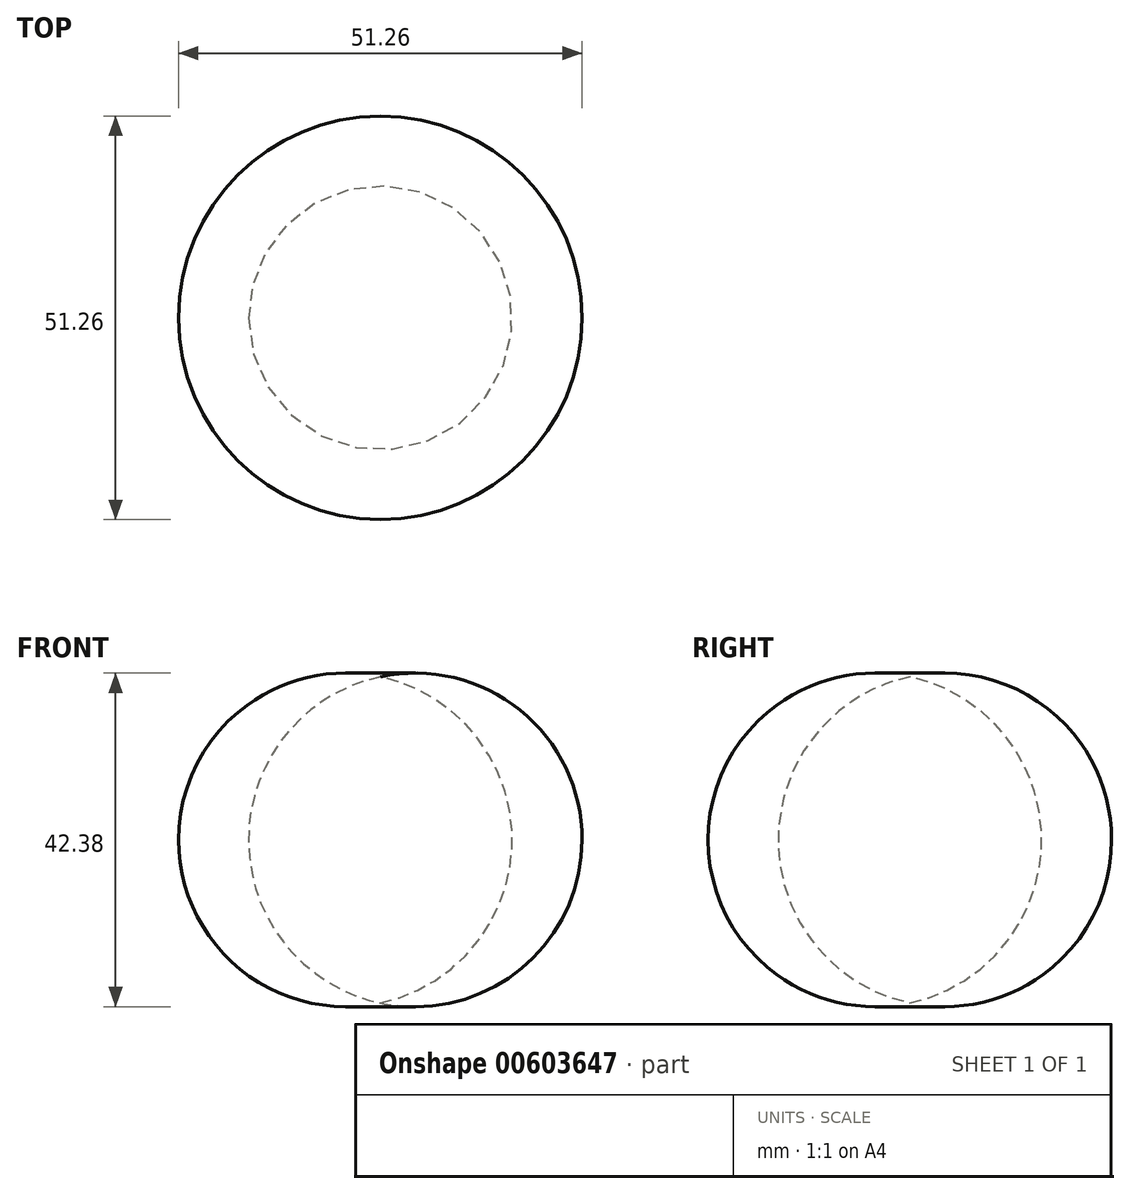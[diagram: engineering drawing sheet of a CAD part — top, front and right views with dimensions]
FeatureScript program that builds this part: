
annotation { "Feature Type Name" : "Feature", "Feature Type Description" : "" }
export const myFeature = defineFeature(function(context is Context, id is Id, definition is map)
    precondition{}
    {
        {
            var Q0;
            Q0=qCreatedBy(makeId("Front.planeOp"),FACE);
            var sketch = newSketch(context, id + "F0", { "sketchPlane" : qUnion([Q0])});
            skLineSegment(sketch, "E0", {"start": v(0, 73.58) * mm, "end": v(0, -52.15) * mm});
            skCircle(sketch, "E1", {"center": v(0, 37.86) * mm, "radius": 19.34 * mm});
            skArc(sketch, "E2", {"start": v(0, -30.72) * mm, "mid": v(25.63, -10) * mm, "end": v(0, 10.72) * mm});
            skSolve(sketch);
        }
        {
            var Q0;
            {var subQ0=sQuery(id+"F0.wireOp",EDGE,"E2");Q0=makeQuery(id+"F0.imprint","IMPRINT",FACE,{"disambiguationData":[TD([[makeQuery(id+"F0.imprint","IMPRINT",EDGE,{"derivedFrom":subQ0}),1.0]])]});}
            var Q1;
            Q1=sQuery(id+"F0.wireOp",EDGE,"E0");
            revolve(context, id + "F1", {"entities" : qUnion([Q0]), "axis" : qUnion([Q1]), "revolveType" : RevolveType.FULL});
        }
    });
